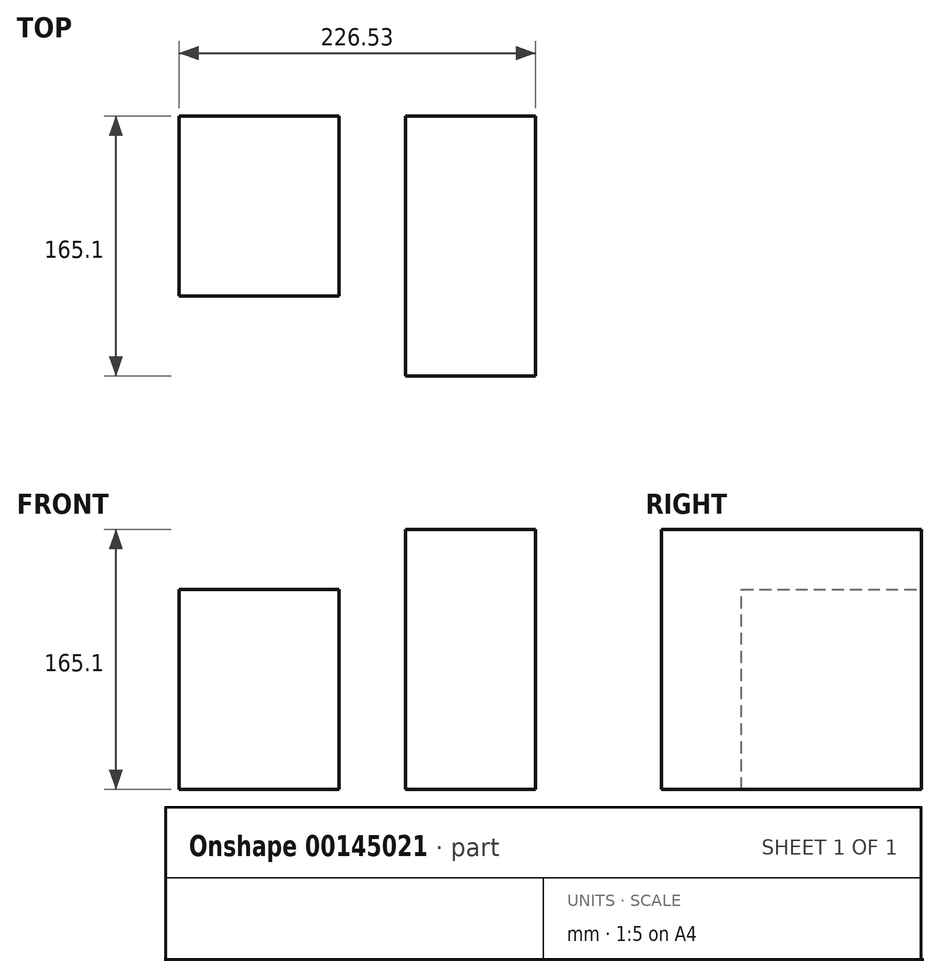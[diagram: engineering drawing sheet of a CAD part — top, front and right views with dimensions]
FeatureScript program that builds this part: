
annotation { "Feature Type Name" : "Feature", "Feature Type Description" : "" }
export const myFeature = defineFeature(function(context is Context, id is Id, definition is map)
    precondition{}
    {
        {
            var Q0;
            Q0=qCreatedBy(makeId("Front.planeOp"),FACE);
            var sketch = newSketch(context, id + "F0", { "sketchPlane" : qUnion([Q0])});
            skLineSegment(sketch, "E0.bottom", {"start": v(0, 0) * mm, "end": v(-101.6, 0) * mm});
            skLineSegment(sketch, "E0.top", {"start": v(0, 127) * mm, "end": v(-101.6, 127) * mm});
            skLineSegment(sketch, "E0.left", {"start": v(0, 0) * mm, "end": v(0, 127) * mm});
            skLineSegment(sketch, "E0.right", {"start": v(-101.6, 0) * mm, "end": v(-101.6, 127) * mm});
            skSolve(sketch);
        }
        {
            var Q0;
            Q0=makeQuery(id+"F0.imprint","IMPRINT",FACE,{"disambiguationData":[TD([[makeQuery(id+"F0.imprint","IMPRINT",EDGE,{"derivedFrom":sQuery(id+"F0.wireOp",EDGE,"E0.bottom")}),-1.0]])]});
            var Q1;
            Q1=makeQuery(id+"F0.imprint","IMPRINT",FACE,{"disambiguationData":[TD([[makeQuery(id+"F0.imprint","IMPRINT",EDGE,{"derivedFrom":sQuery(id+"F0.wireOp",EDGE,"c21f0367-c382-47c1-b640-e65925965c76.sketch_text.stroke-18")}),1.0]])]});
            var Q2;
            Q2=makeQuery(id+"F0.imprint","IMPRINT",FACE,{"disambiguationData":[TD([[makeQuery(id+"F0.imprint","IMPRINT",EDGE,{"derivedFrom":sQuery(id+"F0.wireOp",EDGE,"c21f0367-c382-47c1-b640-e65925965c76.sketch_text.stroke-11")}),1.0]])]});
            var Q3;
            Q3=makeQuery(id+"F0.imprint","IMPRINT",FACE,{"disambiguationData":[TD([[makeQuery(id+"F0.imprint","IMPRINT",EDGE,{"derivedFrom":sQuery(id+"F0.wireOp",EDGE,"c21f0367-c382-47c1-b640-e65925965c76.sketch_text.stroke-44")}),1.0]])]});
            var Q4;
            Q4=makeQuery(id+"F0.imprint","IMPRINT",FACE,{"disambiguationData":[TD([[makeQuery(id+"F0.imprint","IMPRINT",EDGE,{"derivedFrom":sQuery(id+"F0.wireOp",EDGE,"c21f0367-c382-47c1-b640-e65925965c76.sketch_text.stroke-91")}),1.0]])]});
            extrude(context, id + "F1", {"entities" : qUnion([Q0, Q1, Q2, Q3, Q4]), "depth" : 114.3 * mm});
        }
        {
            var Q0;
            Q0=qCreatedBy(makeId("Front.planeOp"),FACE);
            var sketch = newSketch(context, id + "F2", { "sketchPlane" : qUnion([Q0])});
            skLineSegment(sketch, "E1.bottom", {"start": v(42.38, 0) * mm, "end": v(124.93, 0) * mm});
            skLineSegment(sketch, "E1.top", {"start": v(42.38, 165.1) * mm, "end": v(124.93, 165.1) * mm});
            skLineSegment(sketch, "E1.left", {"start": v(42.38, 0) * mm, "end": v(42.38, 165.1) * mm});
            skLineSegment(sketch, "E1.right", {"start": v(124.93, 0) * mm, "end": v(124.93, 165.1) * mm});
            skSolve(sketch);
        }
        {
            var Q0;
            Q0=makeQuery(id+"F2.imprint","IMPRINT",FACE,{"disambiguationData":[TD([[makeQuery(id+"F2.imprint","IMPRINT",EDGE,{"derivedFrom":sQuery(id+"F2.wireOp",EDGE,"E1.bottom")}),1.0]])]});
            extrude(context, id + "F3", {"entities" : qUnion([Q0]), "depth" : 165.1 * mm});
        }
    });
